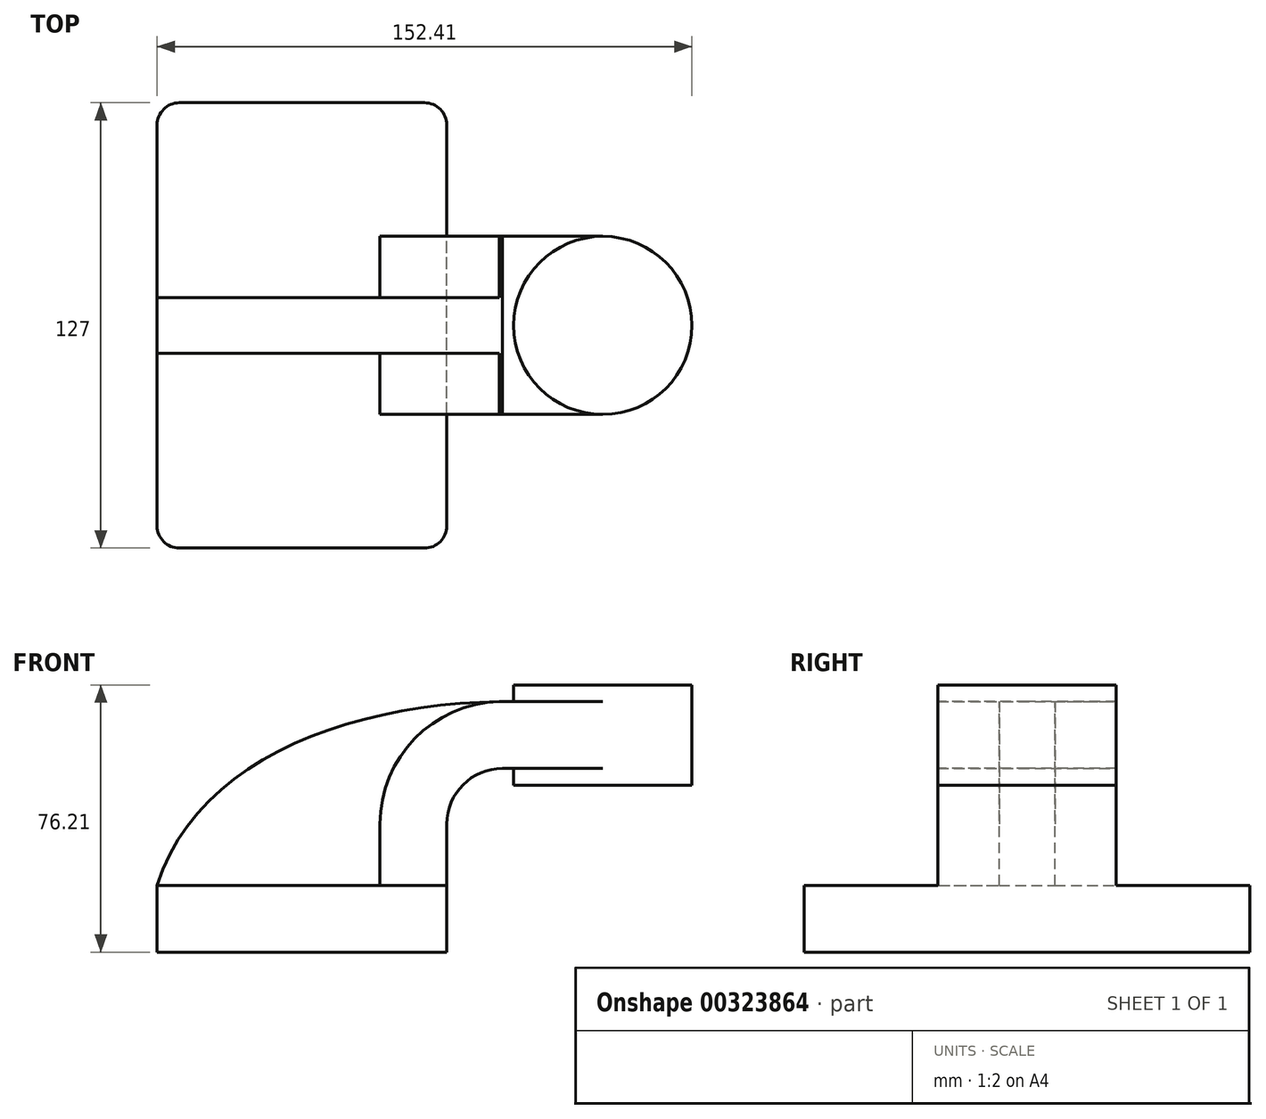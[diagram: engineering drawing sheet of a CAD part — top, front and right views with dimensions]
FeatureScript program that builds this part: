
annotation { "Feature Type Name" : "Feature", "Feature Type Description" : "" }
export const myFeature = defineFeature(function(context is Context, id is Id, definition is map)
    precondition{}
    {
        {
            var Q0;
            Q0=qCreatedBy(makeId("Front.planeOp"),FACE);
            var sketch = newSketch(context, id + "F0", { "sketchPlane" : qUnion([Q0])});
            skLineSegment(sketch, "E0.bottom", {"start": v(41.28, -9.52) * mm, "end": v(-41.28, -9.53) * mm});
            skLineSegment(sketch, "E0.top", {"start": v(41.28, 9.53) * mm, "end": v(-41.28, 9.53) * mm});
            skLineSegment(sketch, "E0.left", {"start": v(41.28, -9.52) * mm, "end": v(41.28, 9.53) * mm});
            skLineSegment(sketch, "E0.right", {"start": v(-41.28, -9.52) * mm, "end": v(-41.28, 9.53) * mm});
            skPoint(sketch, "E0.middle", {"position": v(0, 0) * mm});
            skLineSegment(sketch, "E1.bottom", {"start": v(60.32, 66.68) * mm, "end": v(111.12, 66.68) * mm});
            skLineSegment(sketch, "E1.top", {"start": v(60.32, 38.1) * mm, "end": v(111.12, 38.1) * mm});
            skLineSegment(sketch, "E1.left", {"start": v(60.32, 66.68) * mm, "end": v(60.32, 38.1) * mm});
            skLineSegment(sketch, "E1.right", {"start": v(111.12, 66.68) * mm, "end": v(111.12, 38.1) * mm});
            skPoint(sketch, "E1.middle", {"position": v(85.72, 52.39) * mm});
            skLineSegment(sketch, "E2", {"start": v(41.28, 9.53) * mm, "end": v(41.28, 26.99) * mm});
            skArc(sketch, "E3", {"start": v(41.27, 26.99) * mm, "mid": v(45.92, 38.21) * mm, "end": v(57.15, 42.86) * mm});
            skLineSegment(sketch, "E4", {"start": v(57.15, 42.86) * mm, "end": v(85.72, 42.86) * mm});
            skLineSegment(sketch, "E5.0", {"start": v(57.15, 61.91) * mm, "end": v(85.72, 61.91) * mm});
            skArc(sketch, "E5.1", {"start": v(22.23, 26.99) * mm, "mid": v(32.45, 51.68) * mm, "end": v(57.15, 61.91) * mm});
            skLineSegment(sketch, "E5.2", {"start": v(22.22, 9.53) * mm, "end": v(22.22, 26.99) * mm});
            skLineSegment(sketch, "E6", {"start": v(85.72, 38.1) * mm, "end": v(85.72, 66.68) * mm});
            skFitSpline(sketch, "E7", {"points": [v(-41.28, 9.53) * mm, v(57.15, 61.91) * mm], "startDerivative": vector(33.7, 107.95) * mm, "endDerivative": vector(129.97, 1.4) * mm});
            skSolve(sketch);
        }
        {
            var Q0;
            Q0=makeQuery(id+"F0.imprint","IMPRINT",FACE,{"disambiguationData":[TD([[makeQuery(id+"F0.imprint","IMPRINT",EDGE,{"derivedFrom":sQuery(id+"F0.wireOp",EDGE,"E0.bottom")}),-1.0]])]});
            extrude(context, id + "F1", {"entities" : qUnion([Q0]), "endBound" : BoundingType.SYMMETRIC, "depth" : 127 * mm});
        }
        {
            var Q0;
            {var subQ1=sQuery(id+"F0.wireOp",EDGE,"E2");Q0=makeQuery(id+"F0.imprint","IMPRINT",FACE,{"disambiguationData":[TD([[makeQuery(id+"F0.imprint","IMPRINT",EDGE,{"derivedFrom":subQ1}),1.0]])]});}
            var Q1;
            {var subQ0=sQuery(id+"F0.wireOp",EDGE,"E5.0");var subQ1=sQuery(id+"F0.wireOp",EDGE,"E1.left");var subQ2=makeQuery(id+"F0.imprint","INTERSECT",VERTEX,{"derivedFrom":[subQ1,subQ0]});Q1=makeQuery(id+"F0.imprint","IMPRINT",FACE,{"disambiguationData":[TD([[makeQuery(id+"F0.imprint","IMPRINT",EDGE,{"disambiguationData":[TD([[subQ2,-1.0]])],"derivedFrom":subQ1}),1.0]])]});}
            extrude(context, id + "F2", {"entities" : qUnion([Q0, Q1]), "endBound" : BoundingType.SYMMETRIC, "depth" : 50.8 * mm});
        }
        {
            var Q0;
            {var subQ3=sQuery(id+"F0.wireOp",EDGE,"E5.2");Q0=makeQuery(id+"F0.imprint","IMPRINT",FACE,{"disambiguationData":[TD([[makeQuery(id+"F0.imprint","IMPRINT",EDGE,{"derivedFrom":subQ3}),1.0]])]});}
            extrude(context, id + "F3", {"entities" : qUnion([Q0]), "operationType" : NewBodyOperationType.ADD, "endBound" : BoundingType.SYMMETRIC, "depth" : 15.88 * mm});
        }
        {
            var Q0;
            {var subQ4=sQuery(id+"F0.wireOp",EDGE,"E1.right");Q0=makeQuery(id+"F0.imprint","IMPRINT",FACE,{"disambiguationData":[TD([[makeQuery(id+"F0.imprint","IMPRINT",EDGE,{"derivedFrom":subQ4}),-1.0]])]});}
            var Q1;
            Q1=sQuery(id+"F0.wireOp",EDGE,"E6");
            revolve(context, id + "F4", {"operationType" : NewBodyOperationType.ADD, "entities" : qUnion([Q0]), "axis" : qUnion([Q1]), "revolveType" : RevolveType.FULL});
        }
        {
            var Q0;
            Q0=makeQuery(id+"F1.opExtrude","CAP_EDGE",EDGE,{"disambiguationData":[OSD([sQuery(id+"F0.wireOp",EDGE,"E0.right")])],"isStart":false});
            var Q1;
            Q1=makeQuery(id+"F1.opExtrude","CAP_EDGE",EDGE,{"disambiguationData":[OSD([sQuery(id+"F0.wireOp",EDGE,"E0.left")])],"isStart":false});
            var Q2;
            Q2=makeQuery(id+"F1.opExtrude","CAP_EDGE",EDGE,{"disambiguationData":[OSD([sQuery(id+"F0.wireOp",EDGE,"E0.left")])],"isStart":true});
            var Q3;
            Q3=makeQuery(id+"F1.opExtrude","CAP_EDGE",EDGE,{"disambiguationData":[OSD([sQuery(id+"F0.wireOp",EDGE,"E0.right")])],"isStart":true});
            fillet(context, id + "F5", {"entities" : qUnion([Q0, Q1, Q2, Q3]), "radius" : 6.35 * mm, "tangentPropagation" : true, "allowEdgeOverflow" : false});
        }
    });
